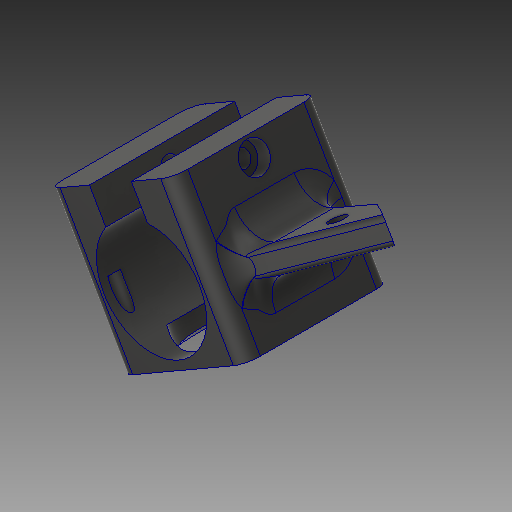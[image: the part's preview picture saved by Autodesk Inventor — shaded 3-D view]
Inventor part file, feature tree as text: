
AUTODESK INVENTOR PART (.ipt)
format: ipt  version: 2019 (Build 230136000, 136)  size: 510,976 bytes
history: native  units: mm
features: plane x1, extrude x1, sketch x1, imported_body x1
ambient origin geometry x8: Origin, YZ Plane, XZ Plane, XY Plane, X Axis, Y Axis, Z Axis, Center Point
bodies: Solid1 (feature_tree)
feature tree (4):
  plane  "Work Plane1"
  extrude  "Extrusion1"  Depth=10.0mm TaperAngle=0.0deg
  sketch  "Sketch1"  dims[d0=25.75mm d1=10.0mm d2=0.0mm]
  imported_body  "Base1"
